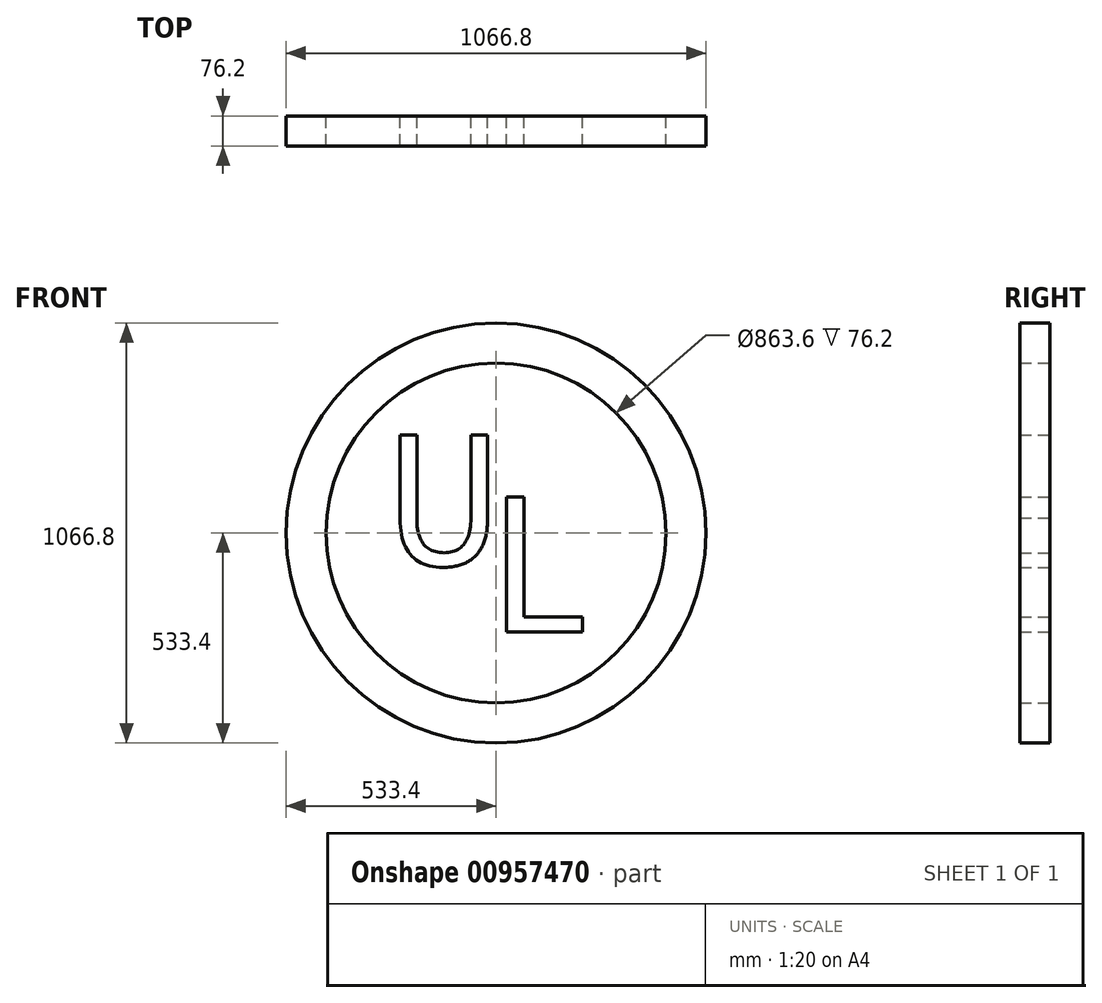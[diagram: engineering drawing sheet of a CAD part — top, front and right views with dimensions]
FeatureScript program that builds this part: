
annotation { "Feature Type Name" : "Feature", "Feature Type Description" : "" }
export const myFeature = defineFeature(function(context is Context, id is Id, definition is map)
    precondition{}
    {
        {
            var Q0;
            Q0=qCreatedBy(makeId("Front.planeOp"),FACE);
            var sketch = newSketch(context, id + "F0", { "sketchPlane" : qUnion([Q0])});
            skCircle(sketch, "E0", {"center": v(0, 0) * mm, "radius": 533.4 * mm});
            skCircle(sketch, "E1", {"center": v(0, 0) * mm, "radius": 431.8 * mm});
            skSolve(sketch);
        }
        {
            var Q0;
            Q0=makeQuery(id+"F0.imprint","IMPRINT",FACE,{"disambiguationData":[TD([[makeQuery(id+"F0.imprint","IMPRINT",EDGE,{"derivedFrom":sQuery(id+"F0.wireOp",EDGE,"E0")}),1.0]])]});
            extrude(context, id + "F1", {"entities" : qUnion([Q0]), "depth" : 76.2 * mm, "offsetDistance" : 25 * mm});
        }
        {
            var Q0;
            Q0=qCreatedBy(makeId("Front.planeOp"),FACE);
            var sketch = newSketch(context, id + "F2", { "sketchPlane" : qUnion([Q0])});
            skText(sketch, "E2", { "text": "U", "fontName": "DroidSansMono.ttf"});
            skText(sketch, "E3", { "text": "L\n", "fontName": "DroidSansMono.ttf"});
            const initialGuessF2  = {"E2": [-0.2718, -0.08257, 1, 0, 0.33437], "E3": [-0.0282, -0.2518, 1, 0, 0.34638]};
            skSetInitialGuess(sketch, initialGuessF2);
            skSolve(sketch);
        }
        {
            var Q0;
            Q0=makeQuery(id+"F2.imprint","IMPRINT",FACE,{"disambiguationData":[TD([[makeQuery(id+"F2.imprint","IMPRINT",EDGE,{"derivedFrom":sQuery(id+"F2.wireOp",EDGE,"E2.sketch_text.stroke-0")}),-1.0]])]});
            var Q1;
            Q1=makeQuery(id+"F2.imprint","IMPRINT",FACE,{"disambiguationData":[TD([[makeQuery(id+"F2.imprint","IMPRINT",EDGE,{"derivedFrom":sQuery(id+"F2.wireOp",EDGE,"E3.sketch_text.stroke-0")}),-1.0]])]});
            extrude(context, id + "F3", {"entities" : qUnion([Q0, Q1]), "depth" : 76.2 * mm, "offsetDistance" : 25 * mm});
        }
    });
